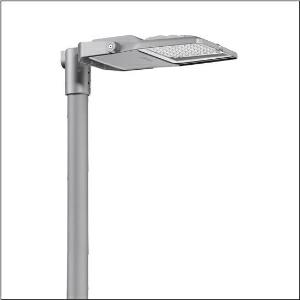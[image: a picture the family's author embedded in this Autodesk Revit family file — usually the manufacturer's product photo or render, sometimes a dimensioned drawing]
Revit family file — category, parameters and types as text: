
# Revit family: floodlight_fl_21_iq_mini___pl61_5xa7771c2c3a_2691
name_source: partatom
category: Lighting Fixtures
units: mm (PartAtom-declared; Revit-internal decimal feet)

## family parameters
Cut with Voids When Loaded = No
Host = Face
Light Source = No
Part Type = Normal
Room Calculation Point = No
Round Connector Dimension = Use Diameter
Shared = No

## types (1)
- --- (1 x LED, 11980 lm, 87.2 W, 3000K)
    Apparent Load = 87 VA
    CIE Flux Codes = 33 65 98 100 100
    Color Rendering = 70
    Color Temperature = 3000K
    Default Elevation = 1800 mm
    Description = Floodlight FL 21 iQ mini, floodlight, primary light control with lens, of PMMA, primary optical cover: protective disc, of toughened safety glass, transparent, light distribution: PL61, light emission: direct distribution, installation type: surface-mounted, LED, High Power LED, rated luminous flux: 11.980lm, luminous efficacy: 137lm/W, light colour: 730, colour temperature: 3000K, control: Auto-Match, Temp-Guard, Lumen-Switch, Night-Set, Smart-Wire, Light-Fading, Desk-Remote (wireless, voltage-free reading and setting of iQ features in the workshop via application-optimized NFC function/RFID function), optimised constant luminous flux control (CLO 2.0), with terminal, 6-pole, mains connection: 220..240V, AC, 50/60Hz, start of lifetime: 87W, end of service life: 92W, reduction: 40W, luminaire housing, of diecast aluminium, powder-coated, Siteco® metallic grey (DB 702S), corrosivity category C5 mid according to DIN EN ISO 12944, sealing non-destructively replaceable, please order mast flange separately, mast bracket, of steel, galvanised, powder-coated, Siteco® metallic grey (DB 702S), protection rating (complete): IP66, insulation class (complete): insulation class II (safety insulation), certification: CE, ENEC, VDE, protection symbol: D, impact resistance: IK08, permissible operating ambient temperature: -40..+40°C, permissible operating ambient temperature for outdoor applications: -40..+50°C, standard: DIN EN 12944, LABS conformity tested according to VDMA 24364:2018-05, packaging unit: 1 piece

Light Distribution: PL61
    Height = 70 mm
    Lamp = 1 x LED
    Lamp Light Flux = 11980 lm
    Lamp Power = 87.2 W
    Lamp count = 1
    Length = 485 mm
    Luminous efficacy = 137 lm/W
    Manufacturer = Siteco
    ModVariant = No
    Model = 5XA7771C2C3A
    Number of Poles = 1
    OnlyDefault = Yes
    Power Factor = 1
    Product Name = Floodlight FL 21 iQ mini | PL61
    Product group = floodlight | pylon annexe
    ProductGroupID = 6200
    Protection Class = Protection class II
    Protection Degree = IP 66
    RLX_Detail_Level = 1
    RLX_Emergency_Light_Flux = 0 lm
    RLX_Emergency_Type = 0
    RLX_Emergency_Type_DB = No
    RlxData = <blob elided: 101453 chars, md5=83fb1260>
    Socket = socket
    Standby Power = 0 W
    System Light Flux = 11980 lm
    System Power = 87 W
    Type Comments = factory setting: luminous flux: 100 % | dim-lin: 254 | 456 mA
    Type Image = l_1007125.jpg
    URL = http://relux.com
    VarID = @adj_144405
    Voltage = 0 V
    Weight = 0.00 kg
    Width = 337 mm

## geometry (parser evidence)
native form markers: Blend x4, Sweep x10
no freeform markers — native parametric forms only
